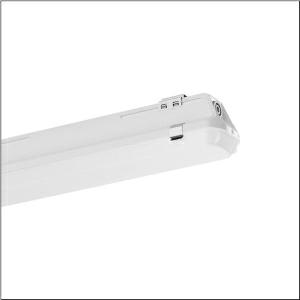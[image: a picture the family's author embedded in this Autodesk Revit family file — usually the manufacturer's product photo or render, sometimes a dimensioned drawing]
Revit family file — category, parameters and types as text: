
# Revit family: monsun_r__21_51fb20dl420j_8a76
name_source: partatom
category: Lighting Fixtures
units: mm (PartAtom-declared; Revit-internal decimal feet)

## family parameters
Cut with Voids When Loaded = No
Host = Face
Light Source = No
Part Type = Normal
Room Calculation Point = No
Round Connector Dimension = Use Diameter
Shared = No

## types (1)
- --- (1 x LED, 2660 lm, 18.4 W, 4000K)
    Apparent Load = 18 VA
    CIE Flux Codes = 45 75 93 94 100
    Color Rendering = 80
    Color Temperature = 4000K
    Default Elevation = 1800 mm
    Description = Monsun® 21, damp-proof luminaire, chain hanger, primary optical cover: enclosure, of PC, light emission: direct distribution, primary light characteristic: symmetric, installation type: suspended mounting, surface-mounted, horizontal mounting, vertical mounting, LED, rated luminous flux: 2.660lm, luminous efficacy: 148lm/W, light colour: 840, colour temperature: 4000K, control gear: ECG DALI, with terminal, 5-pole, max. 2.5mm², mains connection: 220..240V, AC, 50/60Hz, rated input power: 18W, housing, of glass-fibre reinforced plastic, uncoated, bright grey, incl. chain hanger, length: 1.299mm, width: 90mm, height: 88mm, clip for enclosure, of stainless steel (V2A), ceiling mounting element, of stainless steel (V2A), chain hanger, of stainless steel (V2A), protection rating (complete): IP66, insulation class (complete): insulation class I (protective earthing), certification: CE, ENEC, VDE, UKCA, protection symbol: D, impact resistance: IK08, permissible operating ambient temperature: -25..+35°C, standard: EN 50419, EN 60598-2-1, corresponds to IFS (International Featured Standards) requirements for safety and quality in the food industry, for indoor or canopied outdoor use, no direct snow, no direct sun, no direct rain, contact your sales advisor before using the luminaires in applications with unclear chemical exposure, large temperature fluctuations or condensation-forming humidity, LABS conformity tested according to VDMA 24364:2018-05, packaging unit: 1 piece
    Height = 88 mm
    Lamp = 1 x LED
    Lamp Light Flux = 2660 lm
    Lamp Power = 18.4 W
    Lamp count = 1
    Length = 1299 mm
    Luminous efficacy = 145 lm/W
    Manufacturer = Siteco
    ModVariant = No
    Model = 51FB20DL420J
    Mounting Place = Ceiling
    Mounting Type = Surface mounted
    Number of Poles = 1
    OnlyDefault = Yes
    Power Factor = 1
    Product Name = Monsun® 21
    Product group = damp-proof luminaire
    ProductGroupID = 300
    Protection Class = Protection class I
    Protection Degree = IP 66
    RLX_Detail_Level = 1
    RLX_Emergency_Light_Flux = 0 lm
    RLX_Emergency_Type = 0
    RLX_Emergency_Type_DB = No
    RlxData = <blob elided: 94285 chars, md5=34097ca9>
    Socket = socket
    Standby Power = 0 W
    System Light Flux = 2660 lm
    System Power = 18 W
    Type Comments = factory setting: luminous flux: 100 % | dim-lin: 254 | 120 mA
    Type Image = l_1006717.jpg
    URL = http://relux.com
    VarID = @adj_077885
    Voltage = 0 V
    Weight = 0.00 kg
    Width = 90 mm

## geometry (parser evidence)
native form markers: Blend x4, Sweep x12
no freeform markers — native parametric forms only
